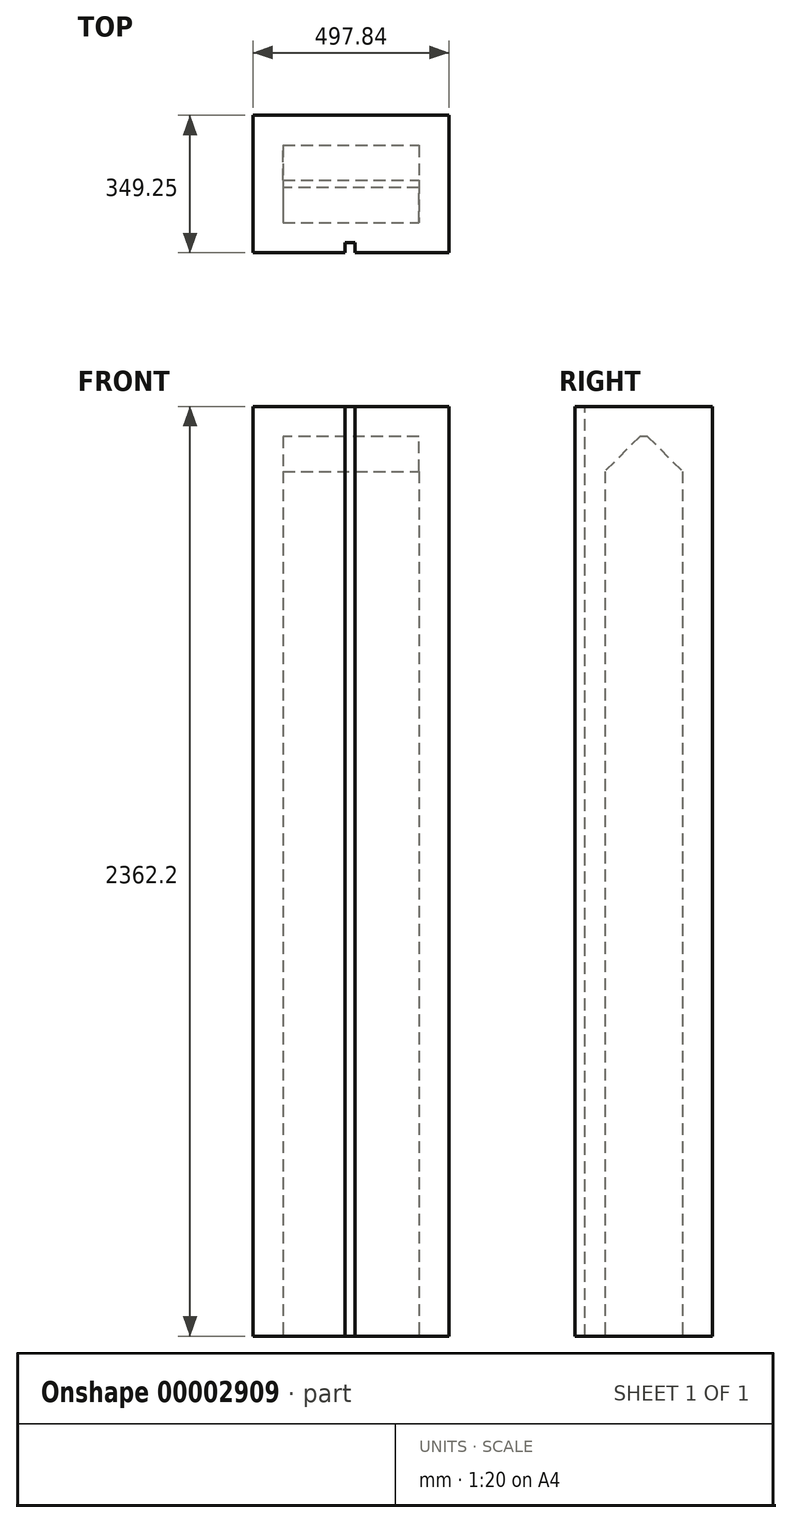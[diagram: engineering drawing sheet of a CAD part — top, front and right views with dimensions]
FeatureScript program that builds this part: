
annotation { "Feature Type Name" : "Feature", "Feature Type Description" : "" }
export const myFeature = defineFeature(function(context is Context, id is Id, definition is map)
    precondition{}
    {
        {
            var Q0;
            Q0=qCreatedBy(makeId("Top.planeOp"),FACE);
            var sketch = newSketch(context, id + "F0", { "sketchPlane" : qUnion([Q0])});
            skLineSegment(sketch, "E0.bottom", {"start": v(-246.14, 158.01) * mm, "end": v(251.7, 158.01) * mm});
            skLineSegment(sketch, "E0.top", {"start": v(-246.14, -191.24) * mm, "end": v(251.7, -191.24) * mm});
            skLineSegment(sketch, "E0.left", {"start": v(-246.14, 158.01) * mm, "end": v(-246.14, -191.24) * mm});
            skLineSegment(sketch, "E0.right", {"start": v(251.7, 158.01) * mm, "end": v(251.7, -191.24) * mm});
            skSolve(sketch);
        }
        {
            var Q0;
            Q0=makeQuery(id+"F0.imprint","IMPRINT",FACE,{"disambiguationData":[TD([[makeQuery(id+"F0.imprint","IMPRINT",EDGE,{"derivedFrom":sQuery(id+"F0.wireOp",EDGE,"E0.bottom")}),-1.0]])]});
            extrude(context, id + "F1", {"entities" : qUnion([Q0]), "depth" : 2362.2 * mm});
        }
        {
            var Q0;
            Q0=makeQuery(id+"F1.opExtrude","SWEPT_FACE",FACE,{"disambiguationData":[OSD([sQuery(id+"F0.wireOp",EDGE,"E0.top")])]});
            var sketch = newSketch(context, id + "F2", { "sketchPlane" : qUnion([Q0])});
            skLineSegment(sketch, "E1.bottom", {"start": v(-12.7, 0) * mm, "end": v(12.7, 0) * mm});
            skLineSegment(sketch, "E1.top", {"start": v(-12.7, 2362.2) * mm, "end": v(12.7, 2362.2) * mm});
            skLineSegment(sketch, "E1.left", {"start": v(-12.7, 0) * mm, "end": v(-12.7, 2362.2) * mm});
            skLineSegment(sketch, "E1.right", {"start": v(12.7, 0) * mm, "end": v(12.7, 2362.2) * mm});
            skSolve(sketch);
        }
        {
            var Q0;
            Q0 = qSketchRegion(id + "F2", true);
            extrude(context, id + "F3", {"entities" : qUnion([Q0]), "operationType" : NewBodyOperationType.REMOVE, "oppositeDirection" : true, "depth" : 25.4 * mm});
        }
        {
            var Q0;
            Q0=makeQuery(id+"F1.opExtrude","CAP_FACE",FACE,{"disambiguationData":[OSD([sQuery(id+"F0.wireOp",EDGE,"E0.bottom"),sQuery(id+"F0.wireOp",EDGE,"E0.top"),sQuery(id+"F0.wireOp",EDGE,"E0.left"),sQuery(id+"F0.wireOp",EDGE,"E0.right")])],"isStart":true});
            shell(context, id + "F4", {"entities" : qUnion([Q0]), "thickness" : 76.2 * mm});
        }
        {
            var Q0;
            Q0=makeQuery(id+"F1.opExtrude","CAP_FACE",FACE,{"disambiguationData":[OSD([sQuery(id+"F0.wireOp",EDGE,"E0.bottom"),sQuery(id+"F0.wireOp",EDGE,"E0.top"),sQuery(id+"F0.wireOp",EDGE,"E0.left"),sQuery(id+"F0.wireOp",EDGE,"E0.right")])],"isStart":true});
            var sketch = newSketch(context, id + "F5", { "sketchPlane" : qUnion([Q0])});
            skLineSegment(sketch, "E2.bottom", {"start": v(-88.9, 89.64) * mm, "end": v(88.9, 89.64) * mm});
            skLineSegment(sketch, "E2.top", {"start": v(-88.9, 115.04) * mm, "end": v(88.9, 115.04) * mm});
            skLineSegment(sketch, "E2.left", {"start": v(-88.9, 89.64) * mm, "end": v(-88.9, 115.04) * mm});
            skLineSegment(sketch, "E2.right", {"start": v(88.9, 89.64) * mm, "end": v(88.9, 115.04) * mm});
            skSolve(sketch);
        }
        {
            var Q0;
            Q0 = qSketchRegion(id + "F5", true);
            var Q1;
            Q1=makeQuery(id+"F4.opShell","OFFSET_FACE",FACE,{"disambiguationData":[OSD([sQuery(id+"F0.wireOp",EDGE,"E0.bottom"),sQuery(id+"F0.wireOp",EDGE,"E0.top"),sQuery(id+"F0.wireOp",EDGE,"E0.left"),sQuery(id+"F0.wireOp",EDGE,"E0.right")])]});
            extrude(context, id + "F6", {"entities" : qUnion([Q0]), "operationType" : NewBodyOperationType.REMOVE, "endBound" : BoundingType.UP_TO_SURFACE, "oppositeDirection" : true, "endBoundEntityFace" : qUnion([Q1]), "depth" : 25.4 * mm});
        }
        {
            var Q0;
            {var subQ0=sQuery(id+"F0.wireOp",EDGE,"E0.top");var subQ1=makeQuery(id+"F1.opExtrude","CAP_EDGE",EDGE,{"disambiguationData":[OSD([subQ0])],"isStart":false});var subQ2=sQuery(id+"F0.wireOp",EDGE,"E0.left");var subQ4=sQuery(id+"F0.wireOp",EDGE,"E0.right");Q0=makeQuery(id+"F6.boolean.opBoolean","MERGE",EDGE,{"derivedFrom":[makeQuery(id+"F4.opShell","OFFSET_EDGE",EDGE,{"disambiguationData":[OSD([subQ0]),TDD([makeQuery(id+"F3.boolean.opBoolean","SPLIT",EDGE,{"disambiguationData":[TD([makeQuery(id+"F1.opExtrude","SWEPT_FACE",FACE,{"disambiguationData":[OSD([subQ2])]})])],"derivedFrom":subQ1})])]}),makeQuery(id+"F4.opShell","OFFSET_EDGE",EDGE,{"disambiguationData":[OSD([subQ0]),TDD([makeQuery(id+"F3.boolean.opBoolean","SPLIT",EDGE,{"disambiguationData":[TD([makeQuery(id+"F1.opExtrude","SWEPT_FACE",FACE,{"disambiguationData":[OSD([subQ4])]})])],"derivedFrom":subQ1})])]}),makeQuery(id+"F6.opExtrude","CAP_EDGE",EDGE,{"disambiguationData":[OSD([sQuery(id+"F5.wireOp",EDGE,"E2.top")])],"isStart":false})]});}
            var Q1;
            {var subQ0=sQuery(id+"F0.wireOp",EDGE,"E0.bottom");Q1=makeQuery(id+"F4.opShell","OFFSET_EDGE",EDGE,{"disambiguationData":[OSD([subQ0]),TDD([makeQuery(id+"F1.opExtrude","CAP_EDGE",EDGE,{"disambiguationData":[OSD([subQ0])],"isStart":false})])]});}
            chamfer(context, id + "F7", {"entities" : qUnion([Q0, Q1]), "width" : 88.9 * mm, "tangentPropagation" : true});
        }
    });
